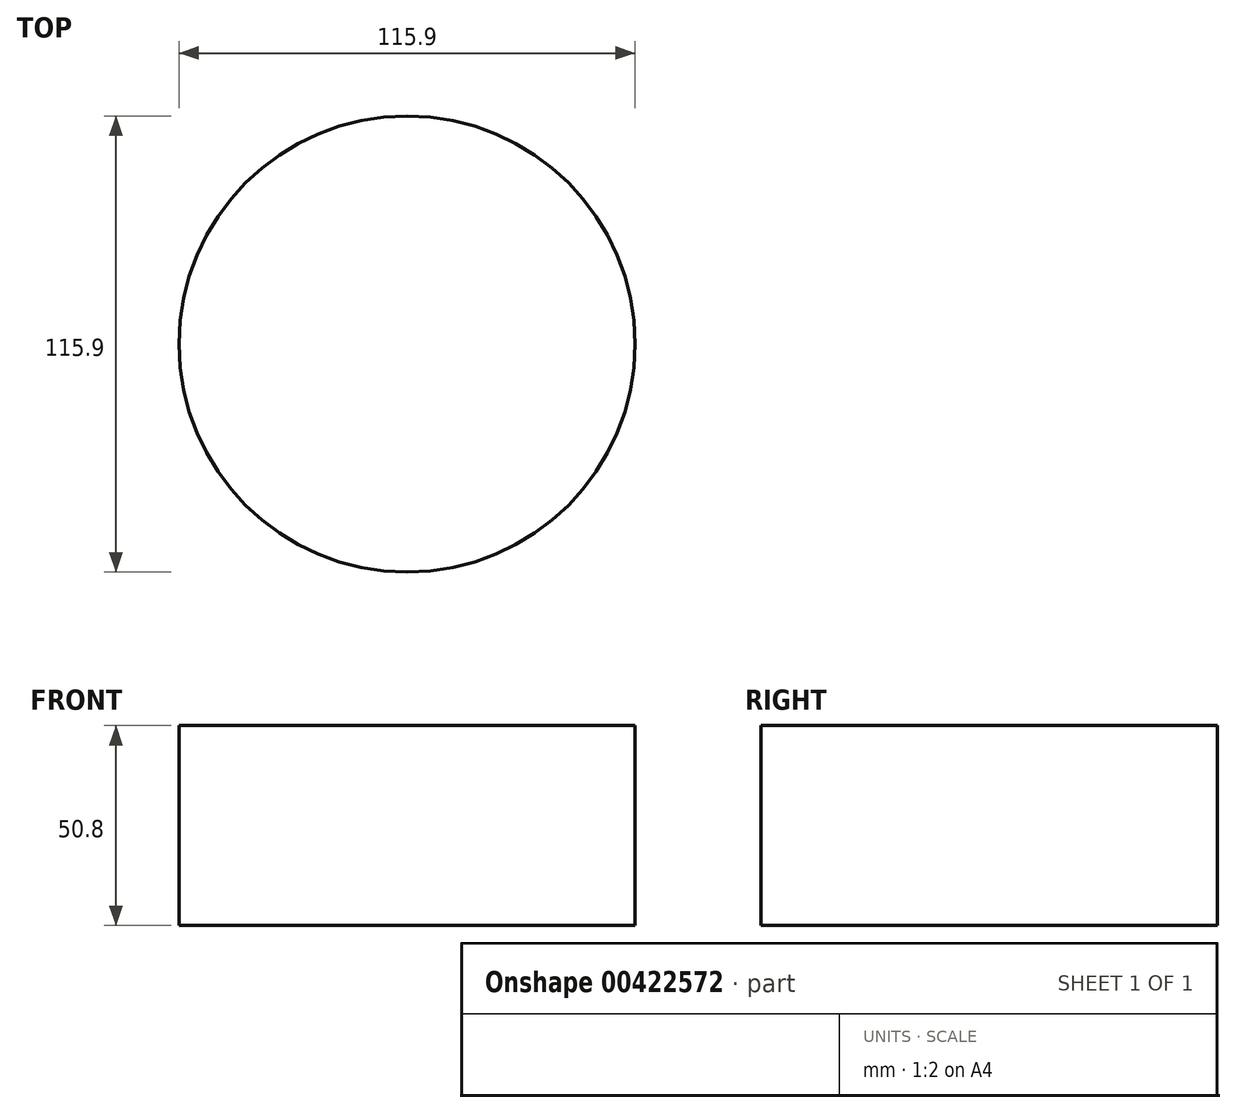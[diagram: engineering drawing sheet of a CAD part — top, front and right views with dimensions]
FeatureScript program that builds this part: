
annotation { "Feature Type Name" : "Feature", "Feature Type Description" : "" }
export const myFeature = defineFeature(function(context is Context, id is Id, definition is map)
    precondition{}
    {
        {
            var Q0;
            Q0=qCreatedBy(makeId("Top.planeOp"),FACE);
            var sketch = newSketch(context, id + "F0", { "sketchPlane" : qUnion([Q0])});
            skCircle(sketch, "E0", {"center": v(0, 0) * mm, "radius": 57.95 * mm});
            skSolve(sketch);
        }
        {
            var Q0;
            Q0=makeQuery(id+"F0.imprint","IMPRINT",FACE,{"disambiguationData":[TD([[makeQuery(id+"F0.imprint","IMPRINT",EDGE,{"derivedFrom":sQuery(id+"F0.wireOp",EDGE,"E0")}),1.0]])]});
            extrude(context, id + "F1", {"entities" : qUnion([Q0]), "endBound" : BoundingType.SYMMETRIC, "depth" : 50.8 * mm});
        }
    });
